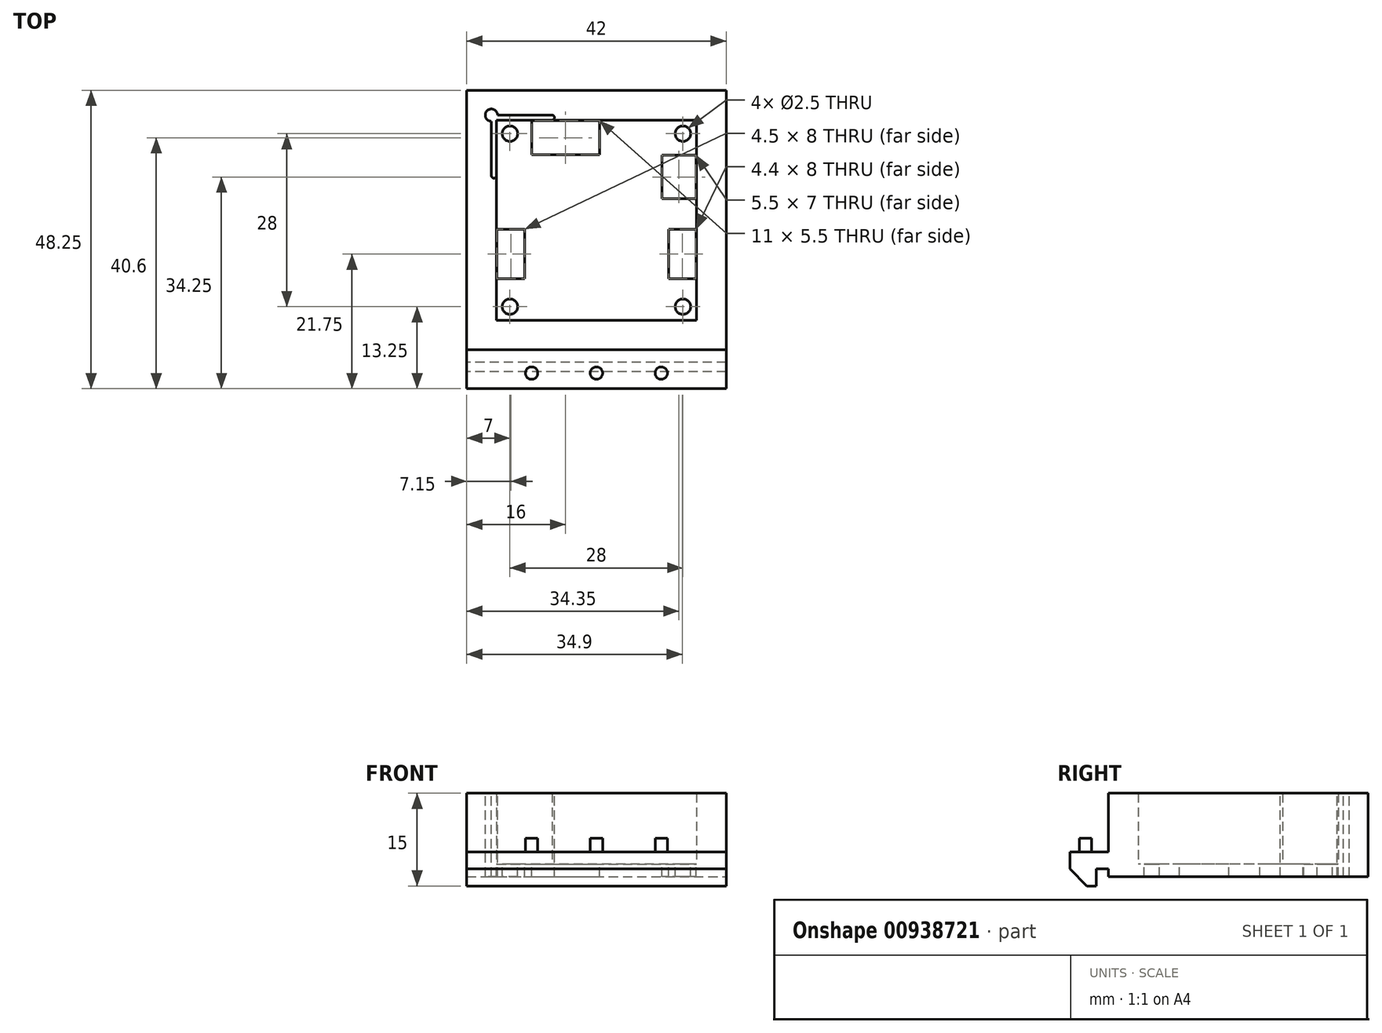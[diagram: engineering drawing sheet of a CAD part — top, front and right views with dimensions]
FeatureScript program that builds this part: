
annotation { "Feature Type Name" : "Feature", "Feature Type Description" : "" }
export const myFeature = defineFeature(function(context is Context, id is Id, definition is map)
    precondition{}
    {
        {
            var Q0;
            Q0=qCreatedBy(makeId("Top.planeOp"),FACE);
            var sketch = newSketch(context, id + "F0", { "sketchPlane" : qUnion([Q0])});
            skLineSegment(sketch, "E0.bottom", {"start": v(19, 19) * mm, "end": v(-19, 19) * mm, "construction": true});
            skLineSegment(sketch, "E0.top", {"start": v(19, -19) * mm, "end": v(2.62, -19) * mm, "construction": true});
            skLineSegment(sketch, "E0.left", {"start": v(19, 19) * mm, "end": v(19, -19) * mm, "construction": true});
            skLineSegment(sketch, "E0.right", {"start": v(-19, 19) * mm, "end": v(-19, -19) * mm, "construction": true});
            skPoint(sketch, "E0.middle", {"position": v(0, 0) * mm});
            skPoint(sketch, "E1", {"position": v(19, 0) * mm});
            skPoint(sketch, "E2", {"position": v(-19, 0) * mm});
            skPoint(sketch, "E3", {"position": v(0, 19) * mm});
            skPoint(sketch, "E4", {"position": v(0, -19) * mm});
            skPoint(sketch, "E5", {"position": v(17, 0) * mm});
            skPoint(sketch, "E6", {"position": v(-17, 0) * mm});
            skLineSegment(sketch, "E7", {"start": v(-19, 0) * mm, "end": v(-17, 0) * mm, "construction": true});
            skLineSegment(sketch, "E8", {"start": v(19, 0) * mm, "end": v(17, 0) * mm, "construction": true});
            skLineSegment(sketch, "E9", {"start": v(0, 19) * mm, "end": v(0, 17) * mm, "construction": true});
            skLineSegment(sketch, "E10", {"start": v(0, -17) * mm, "end": v(0, -19) * mm, "construction": true});
            skPoint(sketch, "E11", {"position": v(-16.2, 16.2) * mm});
            skPoint(sketch, "E12", {"position": v(16.2, -16.2) * mm});
            skPoint(sketch, "E13", {"position": v(16.2, 16.2) * mm});
            skPoint(sketch, "E14", {"position": v(-16.2, -16.2) * mm});
            skPoint(sketch, "E15", {"position": v(17, 4) * mm});
            skPoint(sketch, "E16", {"position": v(17, -4) * mm});
            skPoint(sketch, "E17", {"position": v(16.2, -4) * mm});
            skPoint(sketch, "E18", {"position": v(16.2, 4) * mm});
            skPoint(sketch, "E19", {"position": v(-17, 4) * mm});
            skPoint(sketch, "E20", {"position": v(-16.2, 4) * mm});
            skPoint(sketch, "E21", {"position": v(-17, -4) * mm});
            skPoint(sketch, "E22", {"position": v(-16.2, -4) * mm});
            skPoint(sketch, "E23", {"position": v(-4, 17) * mm});
            skPoint(sketch, "E24", {"position": v(-4, 16.2) * mm});
            skPoint(sketch, "E25", {"position": v(4, 17) * mm});
            skPoint(sketch, "E26", {"position": v(4, 16.2) * mm});
            skPoint(sketch, "E27", {"position": v(-4, -16.2) * mm});
            skPoint(sketch, "E28", {"position": v(4, -16.2) * mm});
            skPoint(sketch, "E29", {"position": v(-4, -17) * mm});
            skPoint(sketch, "E30", {"position": v(4, -17) * mm});
            skLineSegment(sketch, "E31", {"start": v(17, 4) * mm, "end": v(17, -4) * mm});
            skLineSegment(sketch, "E32", {"start": v(16.2, 4) * mm, "end": v(16.2, -4) * mm});
            skLineSegment(sketch, "E33", {"start": v(4, 16.2) * mm, "end": v(-4, 16.2) * mm});
            skLineSegment(sketch, "E34", {"start": v(-4, 17) * mm, "end": v(4, 17) * mm});
            skLineSegment(sketch, "E35", {"start": v(-16.2, 4) * mm, "end": v(-16.2, -4) * mm});
            skLineSegment(sketch, "E36", {"start": v(-17, -4) * mm, "end": v(-17, 4) * mm});
            skLineSegment(sketch, "E37", {"start": v(-4, -16.2) * mm, "end": v(4, -16.2) * mm});
            skLineSegment(sketch, "E38", {"start": v(4, -17) * mm, "end": v(-4, -17) * mm});
            skArc(sketch, "E39", {"start": v(16.2, 4) * mm, "mid": v(16.6, 4.4) * mm, "end": v(17, 4) * mm});
            skArc(sketch, "E40", {"start": v(17, -4) * mm, "mid": v(16.6, -4.4) * mm, "end": v(16.2, -4) * mm});
            skArc(sketch, "E41", {"start": v(4, -16.2) * mm, "mid": v(4.4, -16.6) * mm, "end": v(4, -17) * mm});
            skArc(sketch, "E42", {"start": v(-4, -16.2) * mm, "mid": v(-4.4, -16.6) * mm, "end": v(-4, -17) * mm});
            skArc(sketch, "E43", {"start": v(-17, -4) * mm, "mid": v(-16.6, -4.4) * mm, "end": v(-16.2, -4) * mm});
            skArc(sketch, "E44", {"start": v(-17, 4) * mm, "mid": v(-16.6, 4.4) * mm, "end": v(-16.2, 4) * mm});
            skArc(sketch, "E45", {"start": v(-4, 16.2) * mm, "mid": v(-4.4, 16.6) * mm, "end": v(-4, 17) * mm});
            skArc(sketch, "E46", {"start": v(4, 16.2) * mm, "mid": v(4.4, 16.6) * mm, "end": v(4, 17) * mm});
            skPoint(sketch, "E47", {"position": v(-7.2, 16.2) * mm});
            skPoint(sketch, "E48", {"position": v(-7.2, 17) * mm});
            skPoint(sketch, "E49", {"position": v(-16.2, 7.2) * mm});
            skPoint(sketch, "E50", {"position": v(-17, 7.2) * mm});
            skPoint(sketch, "E51", {"position": v(7.2, 16.2) * mm});
            skPoint(sketch, "E52", {"position": v(7.2, 17) * mm});
            skPoint(sketch, "E53", {"position": v(16.2, 7.2) * mm});
            skPoint(sketch, "E54", {"position": v(17, 7.2) * mm});
            skPoint(sketch, "E55", {"position": v(-17, -7.2) * mm});
            skPoint(sketch, "E56", {"position": v(-16.2, -7.2) * mm});
            skPoint(sketch, "E57", {"position": v(17, -7.2) * mm});
            skPoint(sketch, "E58", {"position": v(16.2, -7.2) * mm});
            skPoint(sketch, "E59", {"position": v(7.2, -17) * mm});
            skPoint(sketch, "E60", {"position": v(7.2, -16.2) * mm});
            skPoint(sketch, "E61", {"position": v(-7.2, -17) * mm});
            skPoint(sketch, "E62", {"position": v(-7.2, -16.2) * mm});
            skLineSegment(sketch, "E63", {"start": v(-7.2, 17) * mm, "end": v(-7.2, 16.2) * mm, "construction": true});
            skLineSegment(sketch, "E64", {"start": v(-17, 7.2) * mm, "end": v(-16.2, 7.2) * mm, "construction": true});
            skLineSegment(sketch, "E65", {"start": v(7.2, 17) * mm, "end": v(7.2, 16.2) * mm, "construction": true});
            skLineSegment(sketch, "E66", {"start": v(16.2, 7.2) * mm, "end": v(17, 7.2) * mm, "construction": true});
            skLineSegment(sketch, "E67", {"start": v(-17, -7.2) * mm, "end": v(-16.2, -7.2) * mm, "construction": true});
            skLineSegment(sketch, "E68", {"start": v(-7.2, -16.2) * mm, "end": v(-7.2, -17) * mm, "construction": true});
            skLineSegment(sketch, "E69", {"start": v(16.2, -7.2) * mm, "end": v(17, -7.2) * mm, "construction": true});
            skLineSegment(sketch, "E70", {"start": v(7.2, -16.2) * mm, "end": v(7.2, -17) * mm, "construction": true});
            skArc(sketch, "E71", {"start": v(-7.2, 17) * mm, "mid": v(-6.8, 16.6) * mm, "end": v(-7.2, 16.2) * mm});
            skArc(sketch, "E72", {"start": v(-16.2, 7.2) * mm, "mid": v(-16.6, 6.8) * mm, "end": v(-17, 7.2) * mm});
            skArc(sketch, "E73", {"start": v(7.2, 17) * mm, "mid": v(6.8, 16.6) * mm, "end": v(7.2, 16.2) * mm});
            skArc(sketch, "E74", {"start": v(17, 7.2) * mm, "mid": v(16.6, 6.8) * mm, "end": v(16.2, 7.2) * mm});
            skArc(sketch, "E75", {"start": v(-16.2, -7.2) * mm, "mid": v(-16.6, -6.8) * mm, "end": v(-17, -7.2) * mm});
            skArc(sketch, "E76", {"start": v(-7.2, -16.2) * mm, "mid": v(-6.8, -16.6) * mm, "end": v(-7.2, -17) * mm});
            skArc(sketch, "E77", {"start": v(7.2, -16.2) * mm, "mid": v(6.8, -16.6) * mm, "end": v(7.2, -17) * mm});
            skArc(sketch, "E78", {"start": v(17, -7.2) * mm, "mid": v(16.6, -6.8) * mm, "end": v(16.2, -7.2) * mm});
            skLineSegment(sketch, "E79", {"start": v(7.2, 17) * mm, "end": v(16.2, 17) * mm});
            skLineSegment(sketch, "E80", {"start": v(7.2, 16.2) * mm, "end": v(16.2, 16.2) * mm});
            skLineSegment(sketch, "E81", {"start": v(16.2, 7.2) * mm, "end": v(16.2, 16.2) * mm});
            skLineSegment(sketch, "E82", {"start": v(17, 16.2) * mm, "end": v(17, 7.2) * mm});
            skLineSegment(sketch, "E83", {"start": v(-16.2, 17) * mm, "end": v(-7.2, 17) * mm});
            skLineSegment(sketch, "E84", {"start": v(-16.2, 16.2) * mm, "end": v(-7.2, 16.2) * mm});
            skLineSegment(sketch, "E85", {"start": v(-16.2, 16.2) * mm, "end": v(-16.2, 7.2) * mm});
            skLineSegment(sketch, "E86", {"start": v(-16.2, -7.2) * mm, "end": v(-16.2, -16.2) * mm});
            skLineSegment(sketch, "E87", {"start": v(-7.2, -16.2) * mm, "end": v(-16.2, -16.2) * mm});
            skLineSegment(sketch, "E88", {"start": v(-17, -7.2) * mm, "end": v(-17, -16.2) * mm});
            skLineSegment(sketch, "E89", {"start": v(-16.2, -17) * mm, "end": v(-7.2, -17) * mm});
            skLineSegment(sketch, "E90", {"start": v(7.2, -17) * mm, "end": v(16.2, -17) * mm});
            skLineSegment(sketch, "E91", {"start": v(7.2, -16.2) * mm, "end": v(16.2, -16.2) * mm});
            skLineSegment(sketch, "E92", {"start": v(17, -16.2) * mm, "end": v(17, -7.2) * mm});
            skLineSegment(sketch, "E93", {"start": v(16.2, -7.2) * mm, "end": v(16.2, -16.2) * mm});
            skLineSegment(sketch, "E94", {"start": v(-17, 7.2) * mm, "end": v(-19, 7.2) * mm, "construction": true});
            skLineSegment(sketch, "E95", {"start": v(-17, -7.2) * mm, "end": v(-19, -7.2) * mm, "construction": true});
            skLineSegment(sketch, "E96", {"start": v(-7.2, 17) * mm, "end": v(-7.2, 19) * mm, "construction": true});
            skLineSegment(sketch, "E97", {"start": v(-7.2, -17) * mm, "end": v(-7.2, -19) * mm, "construction": true});
            skLineSegment(sketch, "E98", {"start": v(7.2, -17) * mm, "end": v(7.2, -19) * mm, "construction": true});
            skLineSegment(sketch, "E99", {"start": v(17, -7.2) * mm, "end": v(19, -7.2) * mm, "construction": true});
            skLineSegment(sketch, "E100", {"start": v(17, 7.2) * mm, "end": v(19, 7.2) * mm, "construction": true});
            skLineSegment(sketch, "E101", {"start": v(7.2, 17) * mm, "end": v(7.2, 19) * mm, "construction": true});
            skPoint(sketch, "E102", {"position": v(-11.7, 17) * mm});
            skPoint(sketch, "E103", {"position": v(-11.7, 16.2) * mm});
            skPoint(sketch, "E104", {"position": v(-17, 11.7) * mm});
            skPoint(sketch, "E105", {"position": v(-16.2, 11.7) * mm});
            skPoint(sketch, "E106", {"position": v(11.7, 17) * mm});
            skPoint(sketch, "E107", {"position": v(11.7, 16.2) * mm});
            skPoint(sketch, "E108", {"position": v(16.2, 11.7) * mm});
            skPoint(sketch, "E109", {"position": v(17, 11.7) * mm});
            skPoint(sketch, "E110", {"position": v(16.2, -11.7) * mm});
            skPoint(sketch, "E111", {"position": v(17, -11.7) * mm});
            skPoint(sketch, "E112", {"position": v(11.7, -16.2) * mm});
            skPoint(sketch, "E113", {"position": v(11.7, -17) * mm});
            skPoint(sketch, "E114", {"position": v(-11.7, -16.2) * mm});
            skPoint(sketch, "E115", {"position": v(-11.7, -17) * mm});
            skPoint(sketch, "E116", {"position": v(-16.2, -11.7) * mm});
            skPoint(sketch, "E117", {"position": v(-17, -11.7) * mm});
            skLineSegment(sketch, "E118", {"start": v(-17, 11.7) * mm, "end": v(-16.2, 11.7) * mm, "construction": true});
            skLineSegment(sketch, "E119", {"start": v(-11.7, 17) * mm, "end": v(-11.7, 16.2) * mm, "construction": true});
            skLineSegment(sketch, "E120", {"start": v(-11.7, -16.2) * mm, "end": v(-11.7, -17) * mm, "construction": true});
            skLineSegment(sketch, "E121", {"start": v(-16.2, -11.7) * mm, "end": v(-17, -11.7) * mm, "construction": true});
            skLineSegment(sketch, "E122", {"start": v(11.7, 17) * mm, "end": v(11.7, 16.2) * mm, "construction": true});
            skLineSegment(sketch, "E123", {"start": v(16.2, 11.7) * mm, "end": v(17, 11.7) * mm, "construction": true});
            skLineSegment(sketch, "E124", {"start": v(11.7, -17) * mm, "end": v(11.7, -16.2) * mm, "construction": true});
            skLineSegment(sketch, "E125", {"start": v(16.2, -11.7) * mm, "end": v(17, -11.7) * mm, "construction": true});
            skPoint(sketch, "E126", {"position": v(-14, 14) * mm});
            skLineSegment(sketch, "E127", {"start": v(-14, 19) * mm, "end": v(-14, 14) * mm, "construction": true});
            skLineSegment(sketch, "E128", {"start": v(-14, 14) * mm, "end": v(-19, 14) * mm, "construction": true});
            skPoint(sketch, "E129", {"position": v(-14, -14) * mm});
            skLineSegment(sketch, "E130", {"start": v(-19, -14) * mm, "end": v(-14, -14) * mm, "construction": true});
            skLineSegment(sketch, "E131", {"start": v(-14, -19) * mm, "end": v(-14, -14) * mm, "construction": true});
            skPoint(sketch, "E132", {"position": v(14, -14) * mm});
            skLineSegment(sketch, "E133", {"start": v(14, -19) * mm, "end": v(14, -14) * mm, "construction": true});
            skLineSegment(sketch, "E134", {"start": v(14, -14) * mm, "end": v(19, -14) * mm, "construction": true});
            skPoint(sketch, "E135", {"position": v(14, 14) * mm});
            skLineSegment(sketch, "E136", {"start": v(14, 19) * mm, "end": v(14, 14) * mm, "construction": true});
            skLineSegment(sketch, "E137", {"start": v(19, 14) * mm, "end": v(14, 14) * mm, "construction": true});
            skPoint(sketch, "E138", {"position": v(16.2, 0) * mm});
            skPoint(sketch, "E139", {"position": v(0, 16.2) * mm});
            skPoint(sketch, "E140", {"position": v(-16.2, 0) * mm});
            skPoint(sketch, "E141", {"position": v(0, -16.2) * mm});
            skLineSegment(sketch, "E142", {"start": v(16.2, 0) * mm, "end": v(17, 0) * mm, "construction": true});
            skLineSegment(sketch, "E143", {"start": v(0, 17) * mm, "end": v(0, 16.2) * mm, "construction": true});
            skLineSegment(sketch, "E144", {"start": v(0, -16.2) * mm, "end": v(0, -17) * mm, "construction": true});
            skLineSegment(sketch, "E145", {"start": v(-17, 0) * mm, "end": v(-16.2, 0) * mm, "construction": true});
            skLineSegment(sketch, "E146", {"start": v(17, 16.2) * mm, "end": v(17, 19) * mm, "construction": true});
            skPoint(sketch, "E147", {"position": v(-17, 17) * mm});
            skPoint(sketch, "E148", {"position": v(17, 17) * mm});
            skPoint(sketch, "E149", {"position": v(-17, -17) * mm});
            skPoint(sketch, "E150", {"position": v(17, -17) * mm});
            skLineSegment(sketch, "E151", {"start": v(16.2, -17) * mm, "end": v(17, -17) * mm, "construction": true});
            skLineSegment(sketch, "E152", {"start": v(17, -17) * mm, "end": v(17, -16.2) * mm, "construction": true});
            skLineSegment(sketch, "E153", {"start": v(17, 16.2) * mm, "end": v(17, 16.25) * mm});
            skPoint(sketch, "E154", {"position": v(-17, 16.2) * mm});
            skLineSegment(sketch, "E155", {"start": v(-16.2, 17) * mm, "end": v(-17, 17) * mm, "construction": true});
            skLineSegment(sketch, "E156", {"start": v(16.2, 4) * mm, "end": v(17, 4) * mm, "construction": true});
            skLineSegment(sketch, "E157", {"start": v(16.2, -4) * mm, "end": v(17, -4) * mm, "construction": true});
            skLineSegment(sketch, "E158", {"start": v(-4, 16.2) * mm, "end": v(-4, 17) * mm, "construction": true});
            skLineSegment(sketch, "E159", {"start": v(4, 16.2) * mm, "end": v(4, 17) * mm, "construction": true});
            skLineSegment(sketch, "E160", {"start": v(-16.2, 4) * mm, "end": v(-17, 4) * mm, "construction": true});
            skLineSegment(sketch, "E161", {"start": v(-16.2, -4) * mm, "end": v(-17, -4) * mm, "construction": true});
            skLineSegment(sketch, "E162", {"start": v(-4, -16.2) * mm, "end": v(-4, -17) * mm, "construction": true});
            skLineSegment(sketch, "E163", {"start": v(4, -16.2) * mm, "end": v(4, -17) * mm, "construction": true});
            skLineSegment(sketch, "E164", {"start": v(-7.2, 17) * mm, "end": v(-4, 17) * mm, "construction": true});
            skLineSegment(sketch, "E165", {"start": v(4, 17) * mm, "end": v(7.2, 17) * mm, "construction": true});
            skLineSegment(sketch, "E166", {"start": v(17, 7.2) * mm, "end": v(17, 4) * mm, "construction": true});
            skLineSegment(sketch, "E167", {"start": v(17, -7.2) * mm, "end": v(17, -4) * mm, "construction": true});
            skLineSegment(sketch, "E168", {"start": v(7.2, -17) * mm, "end": v(4, -17) * mm, "construction": true});
            skLineSegment(sketch, "E169", {"start": v(-4, -17) * mm, "end": v(-7.2, -17) * mm, "construction": true});
            skLineSegment(sketch, "E170", {"start": v(-17, -7.2) * mm, "end": v(-17, -4) * mm, "construction": true});
            skLineSegment(sketch, "E171", {"start": v(-17, 4) * mm, "end": v(-17, 7.2) * mm, "construction": true});
            skCircle(sketch, "E172", {"center": v(14, 14) * mm, "radius": 1.25 * mm});
            skPoint(sketch, "E173", {"position": v(14, 15.25) * mm});
            skPoint(sketch, "E174", {"position": v(15.25, 14) * mm});
            skPoint(sketch, "E175", {"position": v(16.2, 14) * mm});
            skPoint(sketch, "E176", {"position": v(14, 16.2) * mm});
            skCircle(sketch, "E177", {"center": v(-14, 14) * mm, "radius": 1.25 * mm});
            skPoint(sketch, "E178", {"position": v(-14, 15.25) * mm});
            skPoint(sketch, "E179", {"position": v(-15.25, 14) * mm});
            skCircle(sketch, "E180", {"center": v(-14, -14) * mm, "radius": 1.25 * mm});
            skCircle(sketch, "E181", {"center": v(14, -14) * mm, "radius": 1.25 * mm});
            skPoint(sketch, "E182", {"position": v(14, -15.25) * mm});
            skPoint(sketch, "E183", {"position": v(15.25, -14) * mm});
            skPoint(sketch, "E184", {"position": v(-15.25, -14) * mm});
            skPoint(sketch, "E185", {"position": v(-14, -15.25) * mm});
            skLineSegment(sketch, "E186", {"start": v(16.2, 7.2) * mm, "end": v(16.2, 4) * mm});
            skLineSegment(sketch, "E187", {"start": v(-7.2, 16.2) * mm, "end": v(-4, 16.2) * mm});
            skLineSegment(sketch, "E188", {"start": v(-7.2, -16.2) * mm, "end": v(-4, -16.2) * mm});
            skLineSegment(sketch, "E189", {"start": v(4, -16.2) * mm, "end": v(7.2, -16.2) * mm});
            skPoint(sketch, "E190", {"position": v(-16.2, -9) * mm});
            skPoint(sketch, "E191", {"position": v(-16.2, -2) * mm});
            skPoint(sketch, "E192", {"position": v(-16.2, 10) * mm});
            skPoint(sketch, "E193", {"position": v(10, 16.2) * mm});
            skPoint(sketch, "E194", {"position": v(16.2, -1.5) * mm});
            skPoint(sketch, "E195", {"position": v(16.2, -9.5) * mm});
            skPoint(sketch, "E196", {"position": v(10, 19) * mm});
            skPoint(sketch, "E197", {"position": v(-19, 10) * mm});
            skPoint(sketch, "E198", {"position": v(-19, 4) * mm});
            skPoint(sketch, "E199", {"position": v(-19, -2) * mm});
            skPoint(sketch, "E200", {"position": v(-19, -9) * mm});
            skPoint(sketch, "E201", {"position": v(19, -9) * mm});
            skPoint(sketch, "E202", {"position": v(19, -2) * mm});
            skLineSegment(sketch, "E203", {"start": v(0.5, 10.6) * mm, "end": v(0.5, 16.1) * mm});
            skLineSegment(sketch, "E204", {"start": v(-16.1, -9.5) * mm, "end": v(-11.6, -9.5) * mm});
            skLineSegment(sketch, "E205", {"start": v(-11.6, -9.5) * mm, "end": v(-11.6, -1.5) * mm});
            skLineSegment(sketch, "E206", {"start": v(-11.6, -1.5) * mm, "end": v(-16.1, -1.5) * mm});
            skLineSegment(sketch, "E207", {"start": v(16.1, -1.5) * mm, "end": v(11.7, -1.5) * mm});
            skLineSegment(sketch, "E208", {"start": v(11.7, -1.5) * mm, "end": v(11.7, -9.5) * mm});
            skLineSegment(sketch, "E209", {"start": v(11.7, -9.5) * mm, "end": v(16.1, -9.5) * mm});
            skPoint(sketch, "E210", {"position": v(-2.62, -19) * mm});
            skPoint(sketch, "E211", {"position": v(2.62, -19) * mm});
            skLineSegment(sketch, "E212.trimOffspring", {"start": v(-2.62, -19) * mm, "end": v(-19, -19) * mm, "construction": true});
            skLineSegment(sketch, "E213.bottom", {"start": v(-21, -21) * mm, "end": v(21, -21) * mm});
            skLineSegment(sketch, "E213.top", {"start": v(-21, 21) * mm, "end": v(21, 21) * mm});
            skLineSegment(sketch, "E213.left", {"start": v(-21, -21) * mm, "end": v(-21, 21) * mm});
            skLineSegment(sketch, "E213.right", {"start": v(21, -21) * mm, "end": v(21, 21) * mm});
            skPoint(sketch, "E214", {"position": v(2.62, -21) * mm});
            skPoint(sketch, "E215", {"position": v(-2.62, -21) * mm});
            skLineSegment(sketch, "E216", {"start": v(-2.62, -21) * mm, "end": v(-2.62, -19) * mm, "construction": true});
            skLineSegment(sketch, "E217", {"start": v(-16.1, -1.5) * mm, "end": v(-16.1, -9.5) * mm});
            skLineSegment(sketch, "E218", {"start": v(16.1, -1.5) * mm, "end": v(16.1, -9.5) * mm});
            skLineSegment(sketch, "E219", {"start": v(-10.5, 10.6) * mm, "end": v(-10.5, 16.1) * mm});
            skLineSegment(sketch, "E220", {"start": v(-10.5, 16.1) * mm, "end": v(0.5, 16.1) * mm});
            skLineSegment(sketch, "E221", {"start": v(-10.5, 10.6) * mm, "end": v(0.5, 10.6) * mm});
            skPoint(sketch, "E222", {"position": v(10.6, 10.5) * mm});
            skPoint(sketch, "E223", {"position": v(10.6, 3.5) * mm});
            skLineSegment(sketch, "E224", {"start": v(10.6, 3.5) * mm, "end": v(10.6, 10.5) * mm});
            skLineSegment(sketch, "E225", {"start": v(16.1, 10.5) * mm, "end": v(16.1, 3.5) * mm});
            skLineSegment(sketch, "E226", {"start": v(16.1, 3.5) * mm, "end": v(10.6, 3.5) * mm});
            skLineSegment(sketch, "E227", {"start": v(10.6, 10.5) * mm, "end": v(16.1, 10.5) * mm});
            skLineSegment(sketch, "E228", {"start": v(16.2, 17) * mm, "end": v(19, 17) * mm, "construction": true});
            skLineSegment(sketch, "E229", {"start": v(17, -17) * mm, "end": v(19, -17) * mm, "construction": true});
            skLineSegment(sketch, "E230", {"start": v(17, -17) * mm, "end": v(17, -19) * mm, "construction": true});
            skLineSegment(sketch, "E231", {"start": v(-17, 16.2) * mm, "end": v(-17, 17) * mm, "construction": true});
            skLineSegment(sketch, "E232", {"start": v(-17, 16.2) * mm, "end": v(-17, 7.2) * mm});
            skLineSegment(sketch, "E233", {"start": v(-17, 17) * mm, "end": v(-17, 19) * mm, "construction": true});
            skLineSegment(sketch, "E234", {"start": v(-19, 17) * mm, "end": v(-17, 17) * mm, "construction": true});
            skLineSegment(sketch, "E235", {"start": v(-17, -16.2) * mm, "end": v(-17, -17) * mm, "construction": true});
            skLineSegment(sketch, "E236", {"start": v(-16.2, -17) * mm, "end": v(-17, -17) * mm, "construction": true});
            skLineSegment(sketch, "E237", {"start": v(-17, -17) * mm, "end": v(-19, -17) * mm, "construction": true});
            skLineSegment(sketch, "E238", {"start": v(-17, -17) * mm, "end": v(-17, -19) * mm, "construction": true});
            skArc(sketch, "E239", {"start": v(16, -17) * mm, "mid": v(17.7, -17.7) * mm, "end": v(17, -16) * mm});
            skArc(sketch, "E240", {"start": v(-16, 17) * mm, "mid": v(-17.7, 17.7) * mm, "end": v(-17, 16) * mm});
            skArc(sketch, "E241", {"start": v(17, 16) * mm, "mid": v(17.7, 17.7) * mm, "end": v(16, 17) * mm});
            skArc(sketch, "E242", {"start": v(-17, -16) * mm, "mid": v(-17.7, -17.7) * mm, "end": v(-16, -17) * mm});
            skPoint(sketch, "E243", {"position": v(16, 17) * mm});
            skPoint(sketch, "E244", {"position": v(17, 16) * mm});
            skPoint(sketch, "E245", {"position": v(-17, 16) * mm});
            skPoint(sketch, "E246", {"position": v(-16, 17) * mm});
            skPoint(sketch, "E247", {"position": v(-17, -16) * mm});
            skPoint(sketch, "E248", {"position": v(-16, -17) * mm});
            skPoint(sketch, "E249", {"position": v(17, -16) * mm});
            skPoint(sketch, "E250", {"position": v(16, -17) * mm});
            skLineSegment(sketch, "E251", {"start": v(4, 16.2) * mm, "end": v(7.2, 16.2) * mm});
            skLineSegment(sketch, "E252", {"start": v(-16.2, 7.2) * mm, "end": v(-16.2, 4) * mm});
            skLineSegment(sketch, "E253", {"start": v(-16.2, -7.2) * mm, "end": v(-16.2, -4) * mm});
            skLineSegment(sketch, "E254", {"start": v(16.2, -7.2) * mm, "end": v(16.2, -4) * mm});
            skPoint(sketch, "E255", {"position": v(-16.1, -5.5) * mm});
            skPoint(sketch, "E256", {"position": v(-11.6, -5.5) * mm});
            skLineSegment(sketch, "E257", {"start": v(-19, -2) * mm, "end": v(-19, -9) * mm, "construction": true});
            skPoint(sketch, "E258", {"position": v(-19, -5.5) * mm});
            skPoint(sketch, "E259", {"position": v(-10.5, 13.35) * mm});
            skPoint(sketch, "E260", {"position": v(19, 10) * mm});
            skPoint(sketch, "E261", {"position": v(19, 4) * mm});
            skLineSegment(sketch, "E262", {"start": v(19, 10) * mm, "end": v(19, 4) * mm, "construction": true});
            skPoint(sketch, "E263", {"position": v(19, 7) * mm});
            skPoint(sketch, "E264", {"position": v(-10, 19) * mm});
            skLineSegment(sketch, "E265", {"start": v(-10, 19) * mm, "end": v(0, 19) * mm, "construction": true});
            skPoint(sketch, "E266", {"position": v(-5, 19) * mm});
            skPoint(sketch, "E267", {"position": v(-5, 16.1) * mm});
            skPoint(sketch, "E268", {"position": v(16.1, 7) * mm});
            skPoint(sketch, "E269", {"position": v(16.1, -5.5) * mm});
            skLineSegment(sketch, "E270", {"start": v(19, -2) * mm, "end": v(19, -9) * mm, "construction": true});
            skPoint(sketch, "E271", {"position": v(19, -5.5) * mm});
            skSolve(sketch);
        }
        {
            var Q0;
            Q0=qCreatedBy(makeId("Right.planeOp"),FACE);
            var sketch = newSketch(context, id + "F1", { "sketchPlane" : qUnion([Q0])});
            skPoint(sketch, "E272", {"position": v(-21, 0) * mm});
            skPoint(sketch, "E273", {"position": v(-21, -2.75) * mm});
            skLineSegment(sketch, "E274", {"start": v(-21, 0) * mm, "end": v(-23, 0) * mm});
            skLineSegment(sketch, "E275", {"start": v(-23, -2.75) * mm, "end": v(-21, -2.75) * mm});
            skLineSegment(sketch, "E276", {"start": v(-21, 0) * mm, "end": v(-21, -2.75) * mm});
            skLineSegment(sketch, "E277", {"start": v(-23, -2.75) * mm, "end": v(-23, -5.5) * mm});
            skLineSegment(sketch, "E278", {"start": v(-23, -5.5) * mm, "end": v(-24.5, -5.5) * mm});
            skLineSegment(sketch, "E279", {"start": v(-24.5, -5.5) * mm, "end": v(-27.25, -2.75) * mm});
            skLineSegment(sketch, "E280", {"start": v(-27.25, -2.75) * mm, "end": v(-27.25, 0) * mm});
            skLineSegment(sketch, "E281", {"start": v(-27.25, 0) * mm, "end": v(-23, 0) * mm});
            skSolve(sketch);
        }
        {
            var Q0;
            Q0 = qSketchRegion(id + "F0", true);
            var Q1;
            Q1=makeQuery(id+"F0.imprint","IMPRINT",FACE,{"disambiguationData":[TD([[makeQuery(id+"F0.imprint","IMPRINT",EDGE,{"derivedFrom":sQuery(id+"F0.wireOp",EDGE,"E31")}),1.0]])]});
            var Q2;
            Q2=makeQuery(id+"F0.imprint","IMPRINT",FACE,{"disambiguationData":[TD([[makeQuery(id+"F0.imprint","IMPRINT",EDGE,{"derivedFrom":sQuery(id+"F0.wireOp",EDGE,"E33")}),-1.0]])]});
            var Q3;
            Q3=makeQuery(id+"F0.imprint","IMPRINT",FACE,{"disambiguationData":[TD([[makeQuery(id+"F0.imprint","IMPRINT",EDGE,{"derivedFrom":sQuery(id+"F0.wireOp",EDGE,"E73")}),1.0]])]});
            var Q4;
            Q4=makeQuery(id+"F0.imprint","IMPRINT",FACE,{"disambiguationData":[TD([[makeQuery(id+"F0.imprint","IMPRINT",EDGE,{"derivedFrom":sQuery(id+"F0.wireOp",EDGE,"E71")}),-1.0]])]});
            var Q5;
            Q5=makeQuery(id+"F0.imprint","IMPRINT",FACE,{"disambiguationData":[TD([[makeQuery(id+"F0.imprint","IMPRINT",EDGE,{"derivedFrom":sQuery(id+"F0.wireOp",EDGE,"E35")}),-1.0]])]});
            var Q6;
            Q6=makeQuery(id+"F0.imprint","IMPRINT",FACE,{"disambiguationData":[TD([[makeQuery(id+"F0.imprint","IMPRINT",EDGE,{"derivedFrom":sQuery(id+"F0.wireOp",EDGE,"E31")}),-1.0]])]});
            var Q7;
            Q7=makeQuery(id+"F0.imprint","IMPRINT",FACE,{"disambiguationData":[TD([[makeQuery(id+"F0.imprint","IMPRINT",EDGE,{"derivedFrom":sQuery(id+"F0.wireOp",EDGE,"E77")}),1.0]])]});
            var Q8;
            Q8=makeQuery(id+"F0.imprint","IMPRINT",FACE,{"disambiguationData":[TD([[makeQuery(id+"F0.imprint","IMPRINT",EDGE,{"derivedFrom":sQuery(id+"F0.wireOp",EDGE,"E75")}),1.0]])]});
            var Q9;
            Q9=makeQuery(id+"F0.imprint","IMPRINT",FACE,{"disambiguationData":[TD([[makeQuery(id+"F0.imprint","IMPRINT",EDGE,{"derivedFrom":sQuery(id+"F0.wireOp",EDGE,"E37")}),-1.0]])]});
            var Q10;
            Q10=makeQuery(id+"F0.imprint","IMPRINT",FACE,{"disambiguationData":[TD([[makeQuery(id+"F0.imprint","IMPRINT",EDGE,{"derivedFrom":sQuery(id+"F0.wireOp",EDGE,"E32")}),-1.0]])]});
            extrude(context, id + "F2", {"entities" : qUnion([Q0, Q1, Q2, Q3, Q4, Q5, Q6, Q7, Q8, Q9, Q10]), "oppositeDirection" : true, "depth" : 4 * mm, "offsetDistance" : 25 * mm});
        }
        {
            var Q0;
            Q0=makeQuery(id+"F1.imprint","IMPRINT",FACE,{"disambiguationData":[TD([[makeQuery(id+"F1.imprint","IMPRINT",EDGE,{"derivedFrom":sQuery(id+"F1.wireOp",EDGE,"E274")}),1.0]])]});
            extrude(context, id + "F3", {"entities" : qUnion([Q0]), "operationType" : NewBodyOperationType.ADD, "depth" : 21 * mm, "offsetDistance" : 25 * mm});
        }
        {
            var Q0;
            Q0=makeQuery(id+"F3.opExtrude","CAP_FACE",FACE,{"disambiguationData":[OSD([sQuery(id+"F1.wireOp",EDGE,"E274"),sQuery(id+"F1.wireOp",EDGE,"E275"),sQuery(id+"F1.wireOp",EDGE,"E276"),sQuery(id+"F1.wireOp",EDGE,"E277"),sQuery(id+"F1.wireOp",EDGE,"E278"),sQuery(id+"F1.wireOp",EDGE,"E279"),sQuery(id+"F1.wireOp",EDGE,"E280"),sQuery(id+"F1.wireOp",EDGE,"E281")])],"isStart":true});
            extrude(context, id + "F4", {"entities" : qUnion([Q0]), "operationType" : NewBodyOperationType.ADD, "depth" : 21 * mm, "offsetDistance" : 25 * mm});
        }
        {
            var Q0;
            Q0=makeQuery(id+"F0.imprint","IMPRINT",FACE,{"disambiguationData":[TD([[makeQuery(id+"F0.imprint","IMPRINT",EDGE,{"derivedFrom":sQuery(id+"F0.wireOp",EDGE,"E71")}),-1.0]])]});
            var Q1;
            Q1=makeQuery(id+"F0.imprint","IMPRINT",FACE,{"disambiguationData":[TD([[makeQuery(id+"F0.imprint","IMPRINT",EDGE,{"derivedFrom":sQuery(id+"F0.wireOp",EDGE,"E35")}),-1.0]])]});
            var Q2;
            Q2=makeQuery(id+"F0.imprint","IMPRINT",FACE,{"disambiguationData":[TD([[makeQuery(id+"F0.imprint","IMPRINT",EDGE,{"derivedFrom":sQuery(id+"F0.wireOp",EDGE,"E75")}),1.0]])]});
            var Q3;
            Q3=makeQuery(id+"F0.imprint","IMPRINT",FACE,{"disambiguationData":[TD([[makeQuery(id+"F0.imprint","IMPRINT",EDGE,{"derivedFrom":sQuery(id+"F0.wireOp",EDGE,"E33")}),-1.0]])]});
            var Q4;
            Q4=makeQuery(id+"F0.imprint","IMPRINT",FACE,{"disambiguationData":[TD([[makeQuery(id+"F0.imprint","IMPRINT",EDGE,{"derivedFrom":sQuery(id+"F0.wireOp",EDGE,"E73")}),1.0]])]});
            var Q5;
            Q5=makeQuery(id+"F0.imprint","IMPRINT",FACE,{"disambiguationData":[TD([[makeQuery(id+"F0.imprint","IMPRINT",EDGE,{"derivedFrom":sQuery(id+"F0.wireOp",EDGE,"E31")}),-1.0]])]});
            var Q6;
            Q6=makeQuery(id+"F0.imprint","IMPRINT",FACE,{"disambiguationData":[TD([[makeQuery(id+"F0.imprint","IMPRINT",EDGE,{"derivedFrom":sQuery(id+"F0.wireOp",EDGE,"E37")}),-1.0]])]});
            var Q7;
            Q7=makeQuery(id+"F0.imprint","IMPRINT",FACE,{"disambiguationData":[TD([[makeQuery(id+"F0.imprint","IMPRINT",EDGE,{"derivedFrom":sQuery(id+"F0.wireOp",EDGE,"E77")}),1.0]])]});
            extrude(context, id + "F5", {"entities" : qUnion([Q0, Q1, Q2, Q3, Q4, Q5, Q6, Q7]), "operationType" : NewBodyOperationType.ADD, "depth" : 9.5 * mm, "offsetDistance" : 25 * mm});
        }
        {
            var Q0;
            {var subQ0=sQuery(id+"F1.wireOp",EDGE,"E281");var subQ1=sQuery(id+"F1.wireOp",EDGE,"E274");Q0=makeQuery(id+"F4.boolean.opBoolean","MERGE",FACE,{"derivedFrom":[makeQuery(id+"F3.boolean.opBoolean","MERGE",FACE,{"derivedFrom":[makeQuery(id+"F2.opExtrude","CAP_FACE",FACE,{"disambiguationData":[OSD([sQuery(id+"F0.wireOp",EDGE,"E172"),sQuery(id+"F0.wireOp",EDGE,"E177"),sQuery(id+"F0.wireOp",EDGE,"E180"),sQuery(id+"F0.wireOp",EDGE,"E181"),sQuery(id+"F0.wireOp",EDGE,"E203"),sQuery(id+"F0.wireOp",EDGE,"E204"),sQuery(id+"F0.wireOp",EDGE,"E205"),sQuery(id+"F0.wireOp",EDGE,"E206"),sQuery(id+"F0.wireOp",EDGE,"E207"),sQuery(id+"F0.wireOp",EDGE,"E208"),sQuery(id+"F0.wireOp",EDGE,"E209"),sQuery(id+"F0.wireOp",EDGE,"E213.bottom"),sQuery(id+"F0.wireOp",EDGE,"E213.top"),sQuery(id+"F0.wireOp",EDGE,"E213.left"),sQuery(id+"F0.wireOp",EDGE,"E213.right"),sQuery(id+"F0.wireOp",EDGE,"E217"),sQuery(id+"F0.wireOp",EDGE,"E218"),sQuery(id+"F0.wireOp",EDGE,"E219"),sQuery(id+"F0.wireOp",EDGE,"E220"),sQuery(id+"F0.wireOp",EDGE,"E221"),sQuery(id+"F0.wireOp",EDGE,"E224"),sQuery(id+"F0.wireOp",EDGE,"E225"),sQuery(id+"F0.wireOp",EDGE,"E226"),sQuery(id+"F0.wireOp",EDGE,"E227")])],"isStart":true}),makeQuery(id+"F3.opExtrude","SWEPT_FACE",FACE,{"disambiguationData":[OSD([subQ1,subQ0])]})]}),makeQuery(id+"F4.opExtrude","SWEPT_FACE",FACE,{"disambiguationData":[OSD([subQ1,subQ0])]})]});}
            var sketch = newSketch(context, id + "F6", { "sketchPlane" : qUnion([Q0])});
            skPoint(sketch, "E282", {"position": v(0, -17) * mm});
            skPoint(sketch, "E283", {"position": v(0, -18.5) * mm});
            skPoint(sketch, "E284", {"position": v(0, -20.5) * mm});
            skLineSegment(sketch, "E285", {"start": v(0, -20.5) * mm, "end": v(21, -20.5) * mm, "construction": true});
            skLineSegment(sketch, "E286", {"start": v(0, -20.5) * mm, "end": v(-21, -20.5) * mm, "construction": true});
            skLineSegment(sketch, "E287", {"start": v(0, -20.5) * mm, "end": v(0, -24.75) * mm, "construction": true});
            skLineSegment(sketch, "E288", {"start": v(-10.5, -20.5) * mm, "end": v(-10.5, -24.75) * mm, "construction": true});
            skLineSegment(sketch, "E289", {"start": v(10.5, -20.5) * mm, "end": v(10.5, -24.75) * mm, "construction": true});
            skCircle(sketch, "E290", {"center": v(-10.5, -24.75) * mm, "radius": 1 * mm});
            skCircle(sketch, "E291", {"center": v(0, -24.75) * mm, "radius": 1 * mm});
            skCircle(sketch, "E292", {"center": v(10.5, -24.75) * mm, "radius": 1 * mm});
            skLineSegment(sketch, "E293.trimOffspring", {"start": v(-10.5, -25.75) * mm, "end": v(-10.5, -27.25) * mm, "construction": true});
            skLineSegment(sketch, "E294.trimOffspring", {"start": v(0, -25.75) * mm, "end": v(0, -27.25) * mm, "construction": true});
            skLineSegment(sketch, "E295.trimOffspring", {"start": v(10.5, -25.75) * mm, "end": v(10.5, -27.25) * mm, "construction": true});
            skSolve(sketch);
        }
        {
            var Q0;
            Q0 = qSketchRegion(id + "F6", true);
            extrude(context, id + "F7", {"entities" : qUnion([Q0]), "operationType" : NewBodyOperationType.ADD, "depth" : 2.25 * mm, "offsetDistance" : 25 * mm});
        }
        {
            var Q0;
            Q0=makeQuery(id+"F0.imprint","IMPRINT",FACE,{"disambiguationData":[TD([[makeQuery(id+"F0.imprint","IMPRINT",EDGE,{"derivedFrom":sQuery(id+"F0.wireOp",EDGE,"E32")}),-1.0]])]});
            extrude(context, id + "F8", {"entities" : qUnion([Q0]), "operationType" : NewBodyOperationType.REMOVE, "oppositeDirection" : true, "depth" : 2 * mm, "offsetDistance" : 25 * mm});
        }
    });
